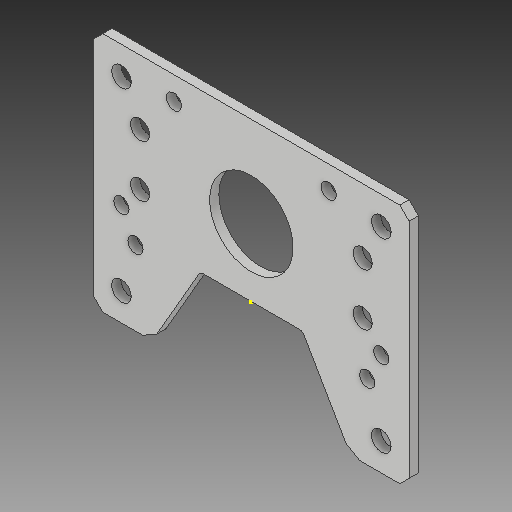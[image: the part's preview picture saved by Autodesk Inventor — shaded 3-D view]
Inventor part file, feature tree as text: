
AUTODESK INVENTOR PART (.ipt)
format: ipt  version: 2017 (Build 210142000, 142)  size: 167,424 bytes
history: native  units: in
note: dims shown in document units (in); Inventor stores cm internally (conversion verified against a paired STEP export)
features: sketch x3, extrude x1, fillet x1
ambient origin geometry x8: Origin, YZ Plane, XZ Plane, XY Plane, X Axis, Y Axis, Z Axis, Center Point
bodies: Solid1 (feature_tree)
feature tree (5):
  sketch  "Sketch1"  dims[d8=1.5in d9=0.35in d10=0.35in]
  sketch  "Sketch2"  dims[d11=1.5in]
  sketch  "Sketch3"  dims[d12=0.35in d13=0.35in d14=0.257in d15=0.257in d16=0.257in d17=0.257in d18=1.0in d19=0.0in]
  extrude  "Extrusion2"  Depth=0.35in
  fillet  "Fillet1"  Radius=0.35in
